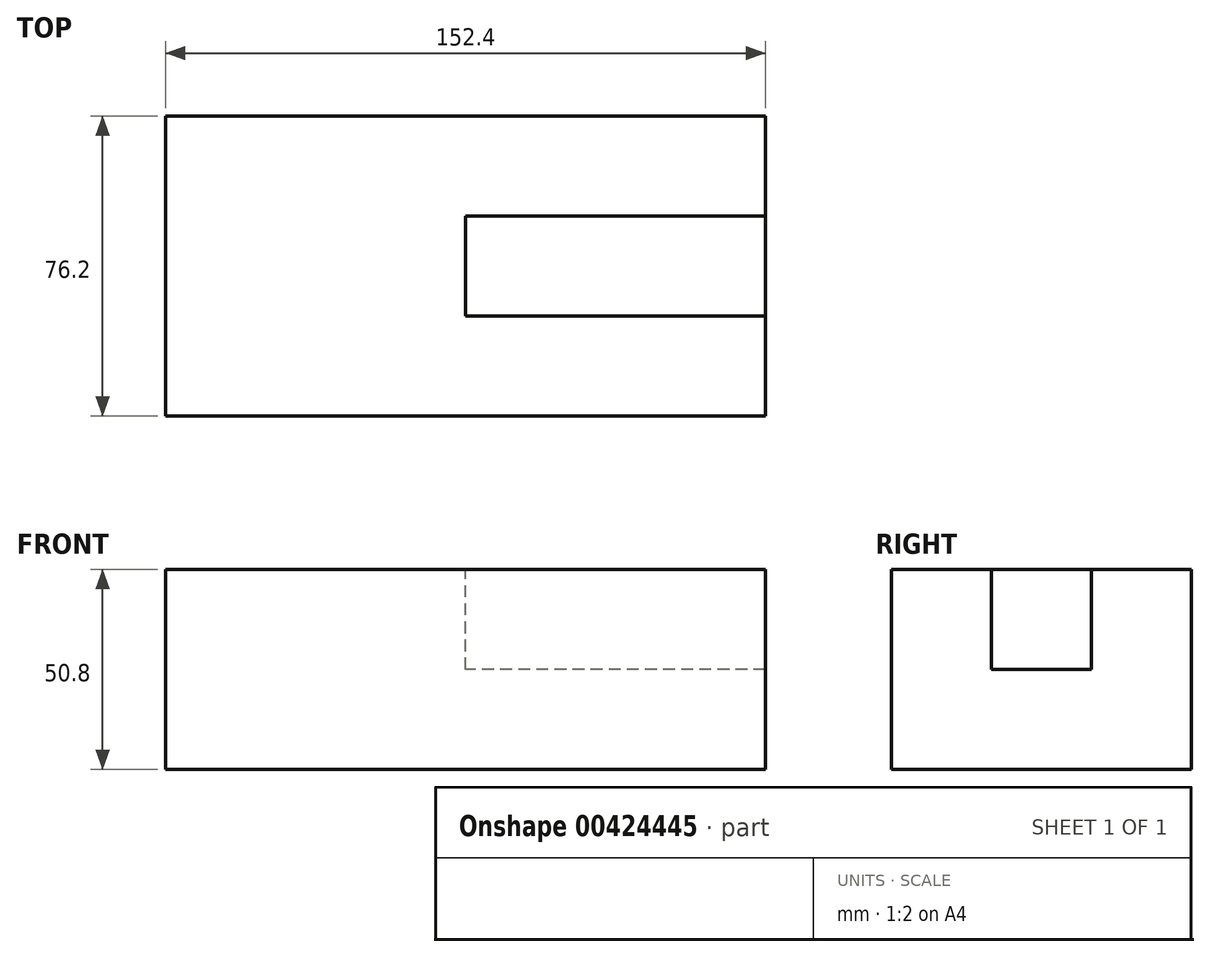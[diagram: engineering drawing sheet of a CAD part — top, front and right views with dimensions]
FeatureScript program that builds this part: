
annotation { "Feature Type Name" : "Feature", "Feature Type Description" : "" }
export const myFeature = defineFeature(function(context is Context, id is Id, definition is map)
    precondition{}
    {
        {
            var Q0;
            Q0=qCreatedBy(makeId("Front.planeOp"),FACE);
            var sketch = newSketch(context, id + "F0", { "sketchPlane" : qUnion([Q0])});
            skLineSegment(sketch, "E0", {"start": v(0, 0) * mm, "end": v(152.4, 0) * mm});
            skLineSegment(sketch, "E1", {"start": v(0, 0) * mm, "end": v(0, 50.8) * mm});
            skLineSegment(sketch, "E2", {"start": v(0, 50.8) * mm, "end": v(152.4, 50.8) * mm});
            skLineSegment(sketch, "E3", {"start": v(152.4, 50.8) * mm, "end": v(152.4, 0) * mm});
            skSolve(sketch);
        }
        {
            var Q0;
            Q0=makeQuery(id+"F0.imprint","IMPRINT",FACE,{"disambiguationData":[TD([[makeQuery(id+"F0.imprint","IMPRINT",EDGE,{"derivedFrom":sQuery(id+"F0.wireOp",EDGE,"E0")}),1.0]])]});
            extrude(context, id + "F1", {"entities" : qUnion([Q0]), "oppositeDirection" : true, "depth" : 76.2 * mm});
        }
        {
            var Q0;
            Q0=makeQuery(id+"F1.opExtrude","SWEPT_FACE",FACE,{"disambiguationData":[OSD([sQuery(id+"F0.wireOp",EDGE,"E2")])]});
            var sketch = newSketch(context, id + "F2", { "sketchPlane" : qUnion([Q0])});
            skLineSegment(sketch, "E4", {"start": v(0, 0) * mm, "end": v(0, 76.2) * mm});
            skLineSegment(sketch, "E5", {"start": v(0, 76.2) * mm, "end": v(152.4, 76.2) * mm});
            skLineSegment(sketch, "E6", {"start": v(152.4, 76.2) * mm, "end": v(152.4, 0) * mm});
            skLineSegment(sketch, "E7", {"start": v(152.4, 0) * mm, "end": v(0, 0) * mm});
            skLineSegment(sketch, "E8", {"start": v(0, 0) * mm, "end": v(76.2, 0) * mm});
            skLineSegment(sketch, "E9", {"start": v(76.2, 0) * mm, "end": v(76.2, 76.2) * mm});
            skLineSegment(sketch, "E10", {"start": v(76.2, 76.2) * mm, "end": v(0, 76.2) * mm});
            skLineSegment(sketch, "E11", {"start": v(0, 76.2) * mm, "end": v(0, 0) * mm});
            skLineSegment(sketch, "E12", {"start": v(76.2, 0) * mm, "end": v(152.4, 0) * mm});
            skLineSegment(sketch, "E13", {"start": v(152.4, 0) * mm, "end": v(152.4, 25.4) * mm});
            skLineSegment(sketch, "E14", {"start": v(152.4, 25.4) * mm, "end": v(76.2, 25.4) * mm});
            skLineSegment(sketch, "E15", {"start": v(152.4, 25.4) * mm, "end": v(152.4, 50.8) * mm});
            skLineSegment(sketch, "E16", {"start": v(152.4, 50.8) * mm, "end": v(76.2, 50.8) * mm});
            skLineSegment(sketch, "E17", {"start": v(152.4, 76.2) * mm, "end": v(152.4, 50.8) * mm});
            skLineSegment(sketch, "E18", {"start": v(152.4, 76.2) * mm, "end": v(76.2, 76.2) * mm});
            skLineSegment(sketch, "E19", {"start": v(76.2, 76.2) * mm, "end": v(76.2, 0) * mm});
            skSolve(sketch);
        }
        {
            var Q0;
            {var subQ2=sQuery(id+"F2.wireOp",EDGE,"E8");Q0=makeQuery(id+"F2.imprint","IMPRINT",FACE,{"disambiguationData":[TD([[makeQuery(id+"F2.imprint","IMPRINT",EDGE,{"derivedFrom":subQ2}),1.0]])]});}
            var Q1;
            {var subQ0=sQuery(id+"F2.wireOp",EDGE,"E14");Q1=makeQuery(id+"F2.imprint","IMPRINT",FACE,{"disambiguationData":[TD([[makeQuery(id+"F2.imprint","IMPRINT",EDGE,{"derivedFrom":subQ0}),-1.0]])]});}
            extrude(context, id + "F3", {"entities" : qUnion([Q0, Q1]), "operationType" : NewBodyOperationType.REMOVE, "oppositeDirection" : true, "depth" : 25.4 * mm});
        }
    });
